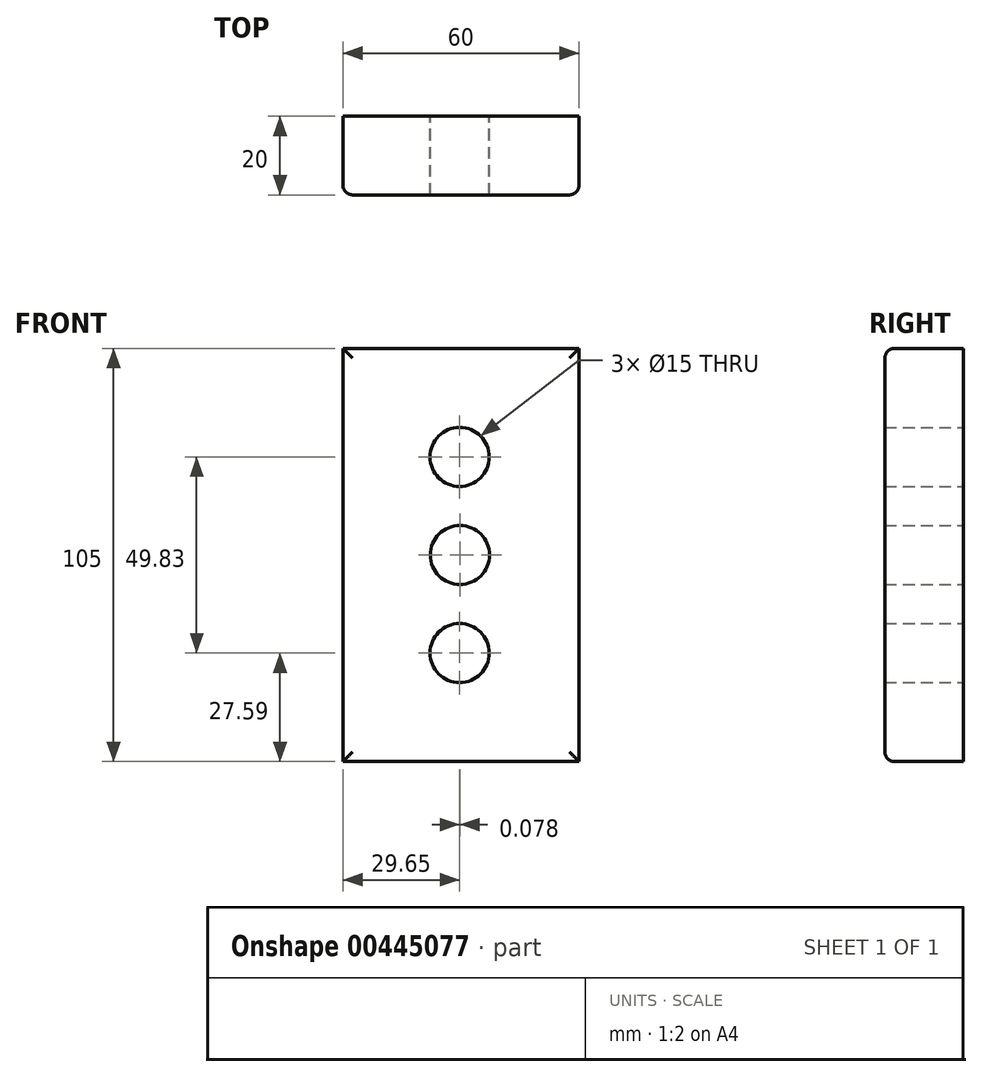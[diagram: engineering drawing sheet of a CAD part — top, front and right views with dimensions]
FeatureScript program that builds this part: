
annotation { "Feature Type Name" : "Feature", "Feature Type Description" : "" }
export const myFeature = defineFeature(function(context is Context, id is Id, definition is map)
    precondition{}
    {
        {
            var Q0;
            Q0=qCreatedBy(makeId("Front.planeOp"),FACE);
            var sketch = newSketch(context, id + "F0", { "sketchPlane" : qUnion([Q0])});
            skLineSegment(sketch, "E0.bottom", {"start": v(-29.65, 45.08) * mm, "end": v(30.35, 45.08) * mm});
            skLineSegment(sketch, "E0.top", {"start": v(-29.65, -59.92) * mm, "end": v(30.35, -59.92) * mm});
            skLineSegment(sketch, "E0.left", {"start": v(-29.65, 45.08) * mm, "end": v(-29.65, -59.92) * mm});
            skLineSegment(sketch, "E0.right", {"start": v(30.35, 45.08) * mm, "end": v(30.35, -59.92) * mm});
            skPoint(sketch, "E1", {"position": v(0.08, -7.42) * mm});
            skCircle(sketch, "E2", {"center": v(0.08, -7.42) * mm, "radius": 7.5 * mm});
            skCircle(sketch, "E3", {"center": v(0, 17.5) * mm, "radius": 7.5 * mm});
            skPoint(sketch, "E3.second.point", {"position": v(0, 25) * mm});
            skPoint(sketch, "E3.third.point", {"position": v(7.3, 19.2) * mm});
            skPoint(sketch, "E4.MirrorP", {"position": v(7.3, -34.03) * mm});
            skCircle(sketch, "E5.MirrorC", {"center": v(0, -32.33) * mm, "radius": 7.5 * mm});
            skPoint(sketch, "E6.MirrorP", {"position": v(0, -39.83) * mm});
            skSolve(sketch);
        }
        {
            var Q0;
            Q0 = qSketchRegion(id + "F0", true);
            extrude(context, id + "F1", {"entities" : qUnion([Q0]), "depth" : 20 * mm});
        }
        {
            var Q0;
            Q0=makeQuery(id+"F1.opExtrude","CAP_EDGE",EDGE,{"disambiguationData":[OSD([sQuery(id+"F0.wireOp",EDGE,"E0.right")])],"isStart":false});
            var Q1;
            Q1=makeQuery(id+"F1.opExtrude","CAP_EDGE",EDGE,{"disambiguationData":[OSD([sQuery(id+"F0.wireOp",EDGE,"E0.bottom")])],"isStart":false});
            var Q2;
            Q2=makeQuery(id+"F1.opExtrude","CAP_EDGE",EDGE,{"disambiguationData":[OSD([sQuery(id+"F0.wireOp",EDGE,"E0.left")])],"isStart":false});
            var Q3;
            Q3=makeQuery(id+"F1.opExtrude","CAP_EDGE",EDGE,{"disambiguationData":[OSD([sQuery(id+"F0.wireOp",EDGE,"E0.top")])],"isStart":false});
            fillet(context, id + "F2", {"entities" : qUnion([Q0, Q1, Q2, Q3]), "radius" : 2.5 * mm, "tangentPropagation" : true, "allowEdgeOverflow" : false});
        }
    });
